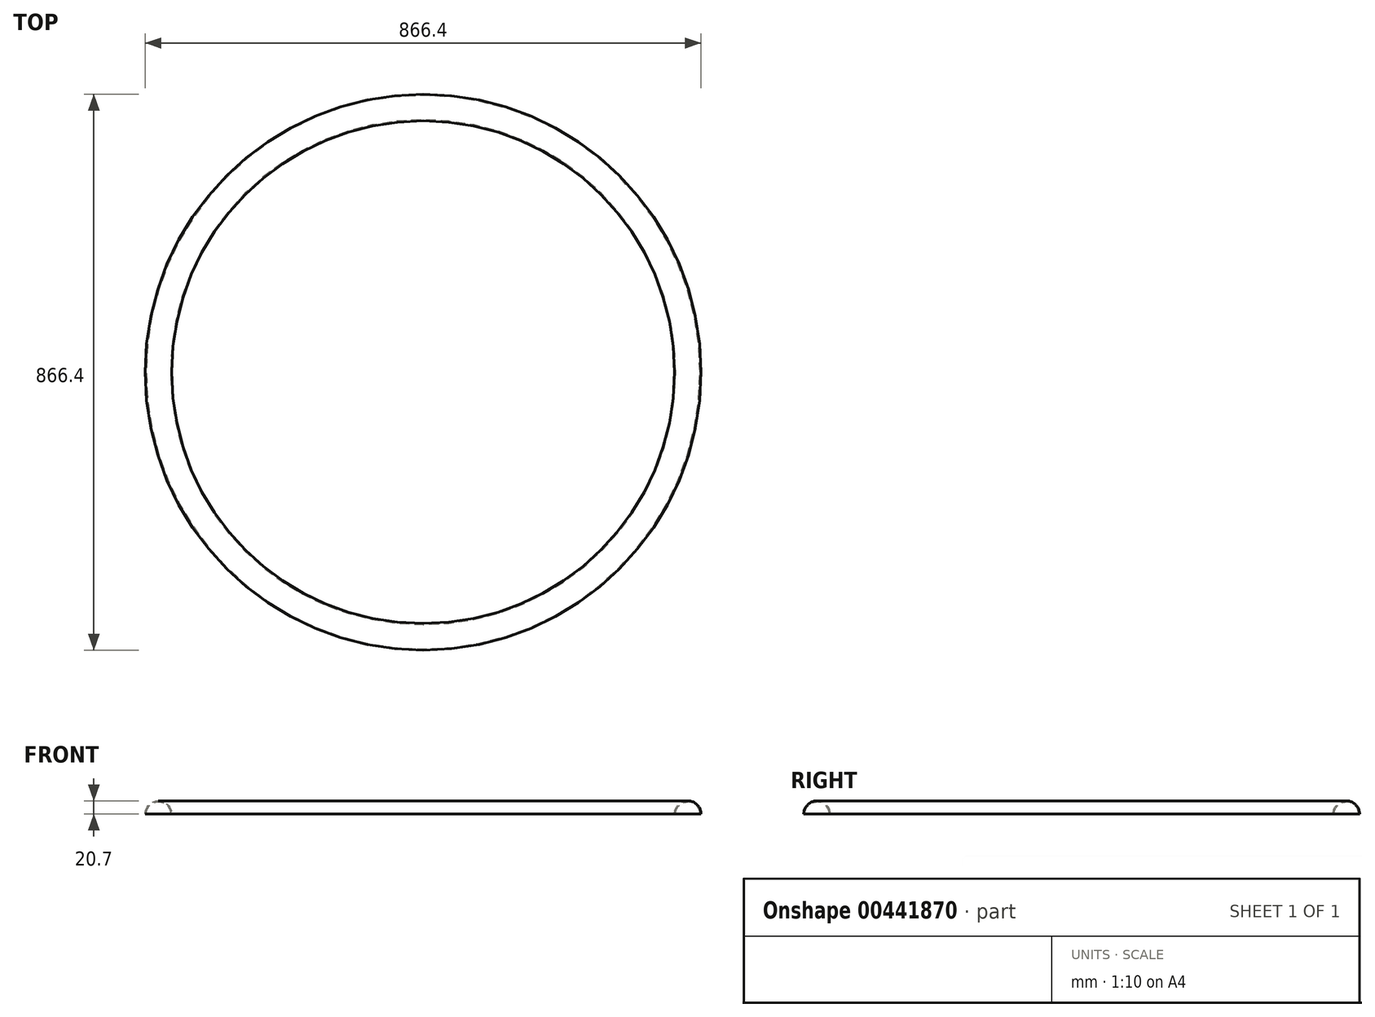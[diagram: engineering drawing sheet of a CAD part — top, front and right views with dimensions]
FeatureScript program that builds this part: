
annotation { "Feature Type Name" : "Feature", "Feature Type Description" : "" }
export const myFeature = defineFeature(function(context is Context, id is Id, definition is map)
    precondition{}
    {
        {
            var Q0;
            Q0=qCreatedBy(makeId("Front.planeOp"),FACE);
            var sketch = newSketch(context, id + "F0", { "sketchPlane" : qUnion([Q0])});
            skArc(sketch, "E0", {"start": v(19.05, 0) * mm, "mid": v(0, 19.05) * mm, "end": v(-19.05, 0) * mm});
            skArc(sketch, "E1.0", {"start": v(20.7, 0) * mm, "mid": v(0, 20.7) * mm, "end": v(-20.7, 0) * mm});
            skLineSegment(sketch, "E2", {"start": v(-38.56, 0) * mm, "end": v(37.9, 0) * mm, "construction": true});
            skLineSegment(sketch, "E3", {"start": v(20.7, 0) * mm, "end": v(19.05, 0) * mm});
            skLineSegment(sketch, "E4", {"start": v(-19.05, 0) * mm, "end": v(-20.7, 0) * mm});
            skSolve(sketch);
        }
        {
            var Q0;
            Q0=qCreatedBy(makeId("Top.planeOp"),FACE);
            var sketch = newSketch(context, id + "F1", { "sketchPlane" : qUnion([Q0])});
            skCircle(sketch, "E5", {"center": v(412.5, 0) * mm, "radius": 412.5 * mm});
            skSolve(sketch);
        }
        {
            var Q0;
            Q0 = qSketchRegion(id + "F0", true);
            var Q1;
            Q1=sQuery(id+"F1.wireOp",EDGE,"E5");
            sweep(context, id + "F2", {"profiles" : qUnion([Q0]), "path" : qUnion([Q1])});
        }
    });
